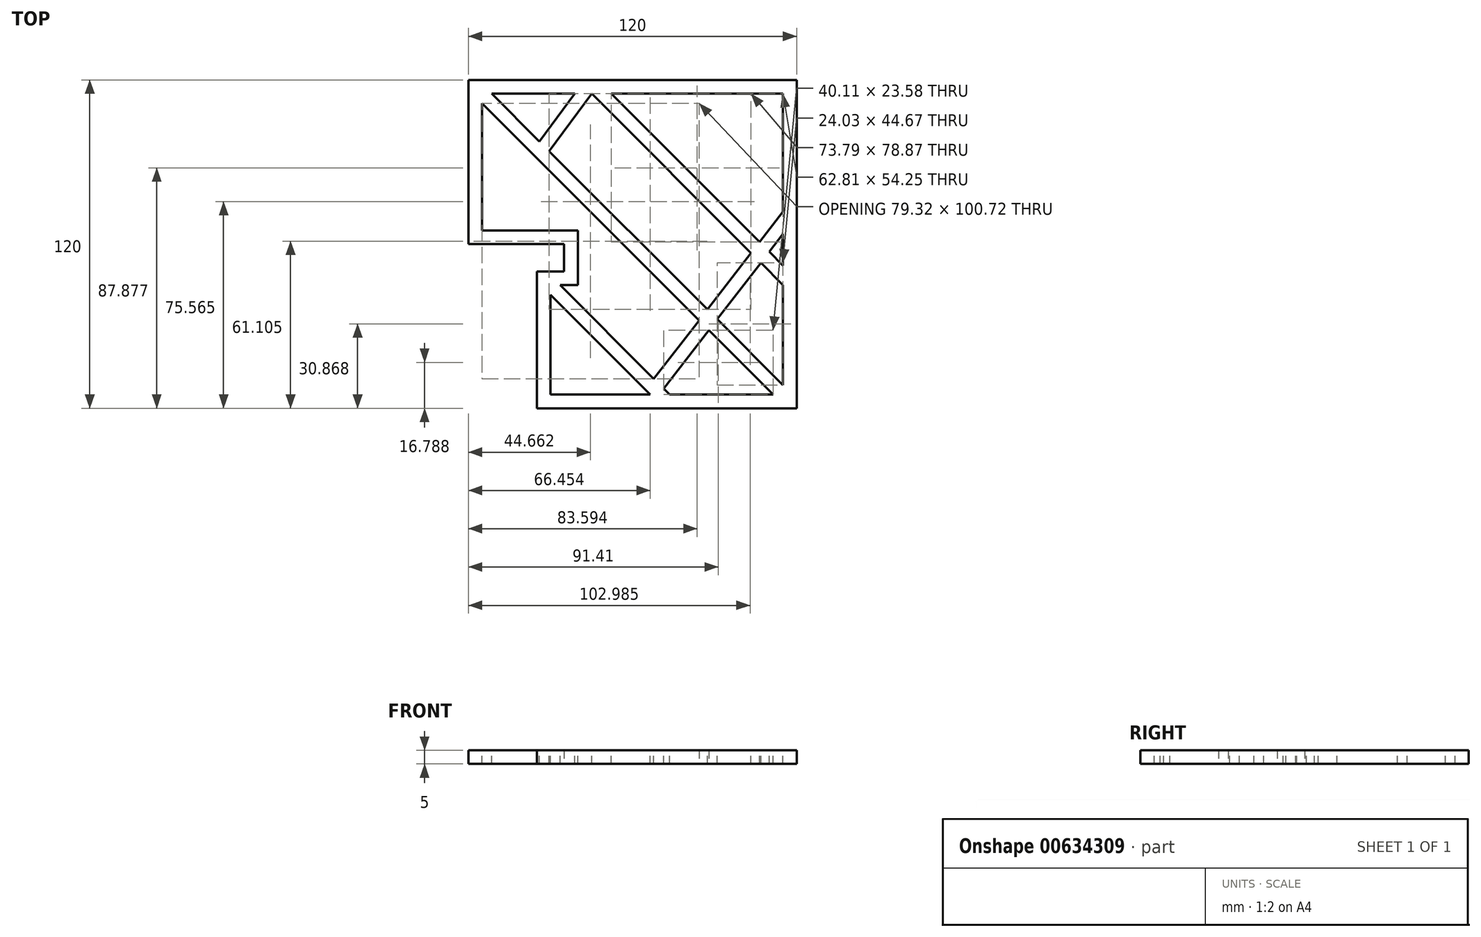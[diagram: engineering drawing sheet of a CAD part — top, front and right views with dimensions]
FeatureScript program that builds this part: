
annotation { "Feature Type Name" : "Feature", "Feature Type Description" : "" }
export const myFeature = defineFeature(function(context is Context, id is Id, definition is map)
    precondition{}
    {
        {
            var Q0;
            Q0=qCreatedBy(makeId("Top.planeOp"),FACE);
            var sketch = newSketch(context, id + "F0", { "sketchPlane" : qUnion([Q0])});
            skLineSegment(sketch, "E0", {"start": v(0, 120) * mm, "end": v(120, 120) * mm});
            skLineSegment(sketch, "E1", {"start": v(120, 120) * mm, "end": v(120, 0) * mm});
            skLineSegment(sketch, "E2", {"start": v(120, 0) * mm, "end": v(25, 0) * mm});
            skLineSegment(sketch, "E3", {"start": v(25, 0) * mm, "end": v(25, 50) * mm});
            skLineSegment(sketch, "E4", {"start": v(25, 50) * mm, "end": v(35, 50) * mm});
            skLineSegment(sketch, "E5", {"start": v(35, 50) * mm, "end": v(35, 60) * mm});
            skLineSegment(sketch, "E6", {"start": v(35, 60) * mm, "end": v(0, 60) * mm});
            skLineSegment(sketch, "E7", {"start": v(0, 60) * mm, "end": v(0, 120) * mm});
            skSolve(sketch);
        }
        {
            var Q0;
            Q0=makeQuery(id+"F0.imprint","IMPRINT",FACE,{"disambiguationData":[TD([[makeQuery(id+"F0.imprint","IMPRINT",EDGE,{"derivedFrom":sQuery(id+"F0.wireOp",EDGE,"E0")}),-1.0]])]});
            extrude(context, id + "F1", {"entities" : qUnion([Q0]), "depth" : 5 * mm, "offsetDistance" : 25 * mm});
        }
        {
            var Q0;
            Q0=makeQuery(id+"F1.opExtrude","CAP_FACE",FACE,{"disambiguationData":[OSD([sQuery(id+"F0.wireOp",EDGE,"E0"),sQuery(id+"F0.wireOp",EDGE,"E1"),sQuery(id+"F0.wireOp",EDGE,"E2"),sQuery(id+"F0.wireOp",EDGE,"E3"),sQuery(id+"F0.wireOp",EDGE,"E4"),sQuery(id+"F0.wireOp",EDGE,"E5"),sQuery(id+"F0.wireOp",EDGE,"E6"),sQuery(id+"F0.wireOp",EDGE,"E7")])],"isStart":false});
            var sketch = newSketch(context, id + "F2", { "sketchPlane" : qUnion([Q0])});
            skLineSegment(sketch, "E8", {"start": v(5, 65) * mm, "end": v(5, 115) * mm});
            skLineSegment(sketch, "E9", {"start": v(5, 115) * mm, "end": v(115, 115) * mm});
            skLineSegment(sketch, "E10", {"start": v(115, 115) * mm, "end": v(115, 5) * mm});
            skLineSegment(sketch, "E11", {"start": v(115, 5) * mm, "end": v(30, 5) * mm});
            skLineSegment(sketch, "E12", {"start": v(30, 5) * mm, "end": v(30, 45) * mm});
            skLineSegment(sketch, "E13", {"start": v(30, 45) * mm, "end": v(40, 45) * mm});
            skLineSegment(sketch, "E14", {"start": v(40, 45) * mm, "end": v(40, 65) * mm});
            skLineSegment(sketch, "E15", {"start": v(40, 65) * mm, "end": v(5, 65) * mm});
            skLineSegment(sketch, "E16", {"start": v(0, 91.25) * mm, "end": v(5, 91.25) * mm, "construction": true});
            skLineSegment(sketch, "E17", {"start": v(21.86, 60) * mm, "end": v(21.86, 65) * mm, "construction": true});
            skLineSegment(sketch, "E18", {"start": v(35, 55) * mm, "end": v(40, 55) * mm, "construction": true});
            skLineSegment(sketch, "E19", {"start": v(54.24, 5) * mm, "end": v(54.24, 0) * mm, "construction": true});
            skLineSegment(sketch, "E20", {"start": v(30, 25) * mm, "end": v(25, 25) * mm, "construction": true});
            skLineSegment(sketch, "E21", {"start": v(115, 35.05) * mm, "end": v(120, 35.05) * mm, "construction": true});
            skLineSegment(sketch, "E22", {"start": v(54.95, 115) * mm, "end": v(54.95, 120) * mm, "construction": true});
            skSolve(sketch);
        }
        {
            var Q0;
            Q0=makeQuery(id+"F2.imprint","IMPRINT",FACE,{"disambiguationData":[TD([[makeQuery(id+"F2.imprint","IMPRINT",EDGE,{"derivedFrom":sQuery(id+"F2.wireOp",EDGE,"E8")}),-1.0]])]});
            extrude(context, id + "F3", {"entities" : qUnion([Q0]), "operationType" : NewBodyOperationType.REMOVE, "oppositeDirection" : true, "depth" : 25 * mm, "offsetDistance" : 25 * mm});
        }
        {
            var Q0;
            Q0=makeQuery(id+"F1.opExtrude","CAP_FACE",FACE,{"disambiguationData":[OSD([sQuery(id+"F0.wireOp",EDGE,"E0"),sQuery(id+"F0.wireOp",EDGE,"E1"),sQuery(id+"F0.wireOp",EDGE,"E2"),sQuery(id+"F0.wireOp",EDGE,"E3"),sQuery(id+"F0.wireOp",EDGE,"E4"),sQuery(id+"F0.wireOp",EDGE,"E5"),sQuery(id+"F0.wireOp",EDGE,"E6"),sQuery(id+"F0.wireOp",EDGE,"E7")])],"isStart":false});
            var sketch = newSketch(context, id + "F4", { "sketchPlane" : qUnion([Q0])});
            skLineSegment(sketch, "E23", {"start": v(115, 5) * mm, "end": v(5, 115) * mm, "construction": true});
            skLineSegment(sketch, "E24", {"start": v(8.54, 115) * mm, "end": v(115, 8.54) * mm});
            skLineSegment(sketch, "E25", {"start": v(115, 8.54) * mm, "end": v(115, 5) * mm});
            skLineSegment(sketch, "E26", {"start": v(111.46, 5) * mm, "end": v(5, 111.46) * mm});
            skLineSegment(sketch, "E27", {"start": v(5, 111.46) * mm, "end": v(5, 115) * mm});
            skLineSegment(sketch, "E28", {"start": v(8.54, 115) * mm, "end": v(6.77, 113.23) * mm, "construction": true});
            skLineSegment(sketch, "E29", {"start": v(6.77, 113.23) * mm, "end": v(5, 111.46) * mm, "construction": true});
            skSolve(sketch);
        }
        {
            var Q0;
            {var subQ3=sQuery(id+"F4.wireOp",EDGE,"E24");Q0=makeQuery(id+"F4.imprint","IMPRINT",FACE,{"disambiguationData":[TD([[makeQuery(id+"F4.imprint","IMPRINT",EDGE,{"derivedFrom":subQ3}),-1.0]])]});}
            extrude(context, id + "F5", {"entities" : qUnion([Q0]), "operationType" : NewBodyOperationType.ADD, "oppositeDirection" : true, "depth" : 5 * mm, "offsetDistance" : 25 * mm});
        }
        {
            var Q0;
            Q0=makeQuery(id+"F5.boolean.opBoolean","MERGE",FACE,{"derivedFrom":[makeQuery(id+"F1.opExtrude","CAP_FACE",FACE,{"disambiguationData":[OSD([sQuery(id+"F0.wireOp",EDGE,"E0"),sQuery(id+"F0.wireOp",EDGE,"E1"),sQuery(id+"F0.wireOp",EDGE,"E2"),sQuery(id+"F0.wireOp",EDGE,"E3"),sQuery(id+"F0.wireOp",EDGE,"E4"),sQuery(id+"F0.wireOp",EDGE,"E5"),sQuery(id+"F0.wireOp",EDGE,"E6"),sQuery(id+"F0.wireOp",EDGE,"E7")])],"isStart":false}),makeQuery(id+"F5.opExtrude","CAP_FACE",FACE,{"disambiguationData":[OSD([sQuery(id+"F2.wireOp",EDGE,"E9"),sQuery(id+"F2.wireOp",EDGE,"E11"),sQuery(id+"F4.wireOp",EDGE,"E24"),sQuery(id+"F4.wireOp",EDGE,"E25"),sQuery(id+"F4.wireOp",EDGE,"E26"),sQuery(id+"F4.wireOp",EDGE,"E27")])],"isStart":true})]});
            var sketch = newSketch(context, id + "F6", { "sketchPlane" : qUnion([Q0])});
            skLineSegment(sketch, "E30", {"start": v(30, 5) * mm, "end": v(115, 115) * mm, "construction": true});
            skLineSegment(sketch, "E31", {"start": v(115, 110.91) * mm, "end": v(33.16, 5) * mm});
            skLineSegment(sketch, "E32", {"start": v(30, 9.09) * mm, "end": v(111.84, 115) * mm});
            skLineSegment(sketch, "E33", {"start": v(82.56, 77.11) * mm, "end": v(84.54, 75.58) * mm, "construction": true});
            skLineSegment(sketch, "E34", {"start": v(84.54, 75.58) * mm, "end": v(86.52, 74.05) * mm, "construction": true});
            skSolve(sketch);
        }
        {
            var Q0;
            {var subQ0=makeQuery(id+"F3.boolean.opBoolean","COPY",EDGE,{"derivedFrom":makeQuery(id+"F3.opExtrude","CAP_EDGE",EDGE,{"disambiguationData":[OSD([sQuery(id+"F2.wireOp",EDGE,"E10")])],"isStart":true})});var subQ5=sQuery(id+"F6.wireOp",EDGE,"E31");var subQ9=makeQuery(id+"F6.imprint","INTERSECT",VERTEX,{"derivedFrom":[subQ0,subQ5]});Q0=makeQuery(id+"F6.imprint","IMPRINT",FACE,{"disambiguationData":[TD([[makeQuery(id+"F6.imprint","IMPRINT",EDGE,{"disambiguationData":[TD([[subQ9,-1.0]])],"derivedFrom":subQ5}),-1.0]])]});}
            var Q1;
            {var subQ0=sQuery(id+"F6.wireOp",EDGE,"E31");var subQ1=makeQuery(id+"F5.opExtrude","CAP_EDGE",EDGE,{"disambiguationData":[OSD([sQuery(id+"F4.wireOp",EDGE,"E24")])],"isStart":true});var subQ2=makeQuery(id+"F6.imprint","INTERSECT",VERTEX,{"derivedFrom":[subQ1,subQ0]});Q1=makeQuery(id+"F6.imprint","IMPRINT",FACE,{"disambiguationData":[TD([[makeQuery(id+"F6.imprint","IMPRINT",EDGE,{"disambiguationData":[TD([[subQ2,-1.0]])],"derivedFrom":subQ0}),-1.0]])]});}
            var Q2;
            {var subQ0=sQuery(id+"F6.wireOp",EDGE,"E31");var subQ7=makeQuery(id+"F3.boolean.opBoolean","COPY",EDGE,{"derivedFrom":makeQuery(id+"F3.opExtrude","CAP_EDGE",EDGE,{"disambiguationData":[OSD([sQuery(id+"F2.wireOp",EDGE,"E11")])],"isStart":true})});var subQ9=makeQuery(id+"F6.imprint","INTERSECT",VERTEX,{"derivedFrom":[subQ7,subQ0]});Q2=makeQuery(id+"F6.imprint","IMPRINT",FACE,{"disambiguationData":[TD([[makeQuery(id+"F6.imprint","IMPRINT",EDGE,{"disambiguationData":[TD([[subQ9,1.0]])],"derivedFrom":subQ0}),-1.0]])]});}
            extrude(context, id + "F7", {"entities" : qUnion([Q0, Q1, Q2]), "operationType" : NewBodyOperationType.ADD, "oppositeDirection" : true, "depth" : 5 * mm, "offsetDistance" : 25 * mm});
        }
        {
            var Q0;
            {var subQ0=sQuery(id+"F2.wireOp",EDGE,"E11");var subQ1=sQuery(id+"F2.wireOp",EDGE,"E9");Q0=makeQuery(id+"F7.boolean.opBoolean","MERGE",FACE,{"derivedFrom":[makeQuery(id+"F5.boolean.opBoolean","MERGE",FACE,{"derivedFrom":[makeQuery(id+"F1.opExtrude","CAP_FACE",FACE,{"disambiguationData":[OSD([sQuery(id+"F0.wireOp",EDGE,"E0"),sQuery(id+"F0.wireOp",EDGE,"E1"),sQuery(id+"F0.wireOp",EDGE,"E2"),sQuery(id+"F0.wireOp",EDGE,"E3"),sQuery(id+"F0.wireOp",EDGE,"E4"),sQuery(id+"F0.wireOp",EDGE,"E5"),sQuery(id+"F0.wireOp",EDGE,"E6"),sQuery(id+"F0.wireOp",EDGE,"E7")])],"isStart":false}),makeQuery(id+"F5.opExtrude","CAP_FACE",FACE,{"disambiguationData":[OSD([subQ1,subQ0,sQuery(id+"F4.wireOp",EDGE,"E24"),sQuery(id+"F4.wireOp",EDGE,"E25"),sQuery(id+"F4.wireOp",EDGE,"E26"),sQuery(id+"F4.wireOp",EDGE,"E27")])],"isStart":true})]}),makeQuery(id+"F7.opExtrude","CAP_FACE",FACE,{"disambiguationData":[OSD([subQ1,sQuery(id+"F2.wireOp",EDGE,"E10"),subQ0,sQuery(id+"F2.wireOp",EDGE,"E12"),sQuery(id+"F6.wireOp",EDGE,"E31"),sQuery(id+"F6.wireOp",EDGE,"E32")])],"isStart":true})]});}
            var sketch = newSketch(context, id + "F8", { "sketchPlane" : qUnion([Q0])});
            skLineSegment(sketch, "E35", {"start": v(40, 65) * mm, "end": v(78.64, 115) * mm, "construction": true});
            skLineSegment(sketch, "E36", {"start": v(40, 60.91) * mm, "end": v(81.8, 115) * mm});
            skLineSegment(sketch, "E37", {"start": v(75.48, 115) * mm, "end": v(36.84, 65) * mm});
            skLineSegment(sketch, "E38", {"start": v(65.07, 97.45) * mm, "end": v(67.05, 95.92) * mm, "construction": true});
            skLineSegment(sketch, "E39", {"start": v(61.65, 97.1) * mm, "end": v(63.63, 95.57) * mm, "construction": true});
            skSolve(sketch);
        }
        {
            var Q0;
            {var subQ0=sQuery(id+"F8.wireOp",EDGE,"E36");var subQ1=sQuery(id+"F2.wireOp",EDGE,"E9");var subQ2=makeQuery(id+"F3.boolean.opBoolean","COPY",EDGE,{"derivedFrom":makeQuery(id+"F3.opExtrude","CAP_EDGE",EDGE,{"disambiguationData":[OSD([subQ1])],"isStart":true})});var subQ3=makeQuery(id+"F8.imprint","INTERSECT",VERTEX,{"derivedFrom":[subQ2,subQ0]});Q0=makeQuery(id+"F8.imprint","IMPRINT",FACE,{"disambiguationData":[TD([[makeQuery(id+"F8.imprint","IMPRINT",EDGE,{"disambiguationData":[TD([[subQ3,1.0]])],"derivedFrom":subQ2}),-1.0]])]});}
            var Q1;
            {var subQ0=sQuery(id+"F8.wireOp",EDGE,"E36");var subQ1=sQuery(id+"F4.wireOp",EDGE,"E26");var subQ10=makeQuery(id+"F7.boolean.opBoolean","SPLIT",EDGE,{"disambiguationData":[TD([makeQuery(id+"F3.boolean.opBoolean","COPY",FACE,{"derivedFrom":makeQuery(id+"F3.opExtrude","SWEPT_FACE",FACE,{"disambiguationData":[OSD([sQuery(id+"F2.wireOp",EDGE,"E8")])]})})])],"derivedFrom":makeQuery(id+"F5.opExtrude","CAP_EDGE",EDGE,{"disambiguationData":[OSD([subQ1])],"isStart":true})});var subQ11=makeQuery(id+"F8.imprint","INTERSECT",VERTEX,{"derivedFrom":[subQ10,subQ0]});Q1=makeQuery(id+"F8.imprint","IMPRINT",FACE,{"disambiguationData":[TD([[makeQuery(id+"F8.imprint","IMPRINT",EDGE,{"disambiguationData":[TD([[subQ11,-1.0]])],"derivedFrom":subQ0}),1.0]])]});}
            var Q2;
            {var subQ0=makeQuery(id+"F3.boolean.opBoolean","COPY",EDGE,{"derivedFrom":makeQuery(id+"F3.opExtrude","CAP_EDGE",EDGE,{"disambiguationData":[OSD([sQuery(id+"F2.wireOp",EDGE,"E15")])],"isStart":true})});var subQ1=makeQuery(id+"F3.boolean.opBoolean","COPY",EDGE,{"derivedFrom":makeQuery(id+"F3.opExtrude","CAP_EDGE",EDGE,{"disambiguationData":[OSD([sQuery(id+"F2.wireOp",EDGE,"E14")])],"isStart":true})});var subQ2=makeQuery(id+"F8.imprint","INTERSECT",VERTEX,{"derivedFrom":[subQ1,subQ0]});Q2=makeQuery(id+"F8.imprint","IMPRINT",FACE,{"disambiguationData":[TD([[makeQuery(id+"F8.imprint","IMPRINT",EDGE,{"disambiguationData":[TD([[subQ2,1.0]])],"derivedFrom":subQ1}),-1.0]])]});}
            extrude(context, id + "F9", {"entities" : qUnion([Q0, Q1, Q2]), "operationType" : NewBodyOperationType.ADD, "oppositeDirection" : true, "depth" : 5 * mm, "offsetDistance" : 25 * mm});
        }
        {
            var Q0;
            {var subQ0=sQuery(id+"F2.wireOp",EDGE,"E9");var subQ1=sQuery(id+"F2.wireOp",EDGE,"E11");Q0=makeQuery(id+"F9.boolean.opBoolean","MERGE",FACE,{"derivedFrom":[makeQuery(id+"F7.boolean.opBoolean","MERGE",FACE,{"derivedFrom":[makeQuery(id+"F5.boolean.opBoolean","MERGE",FACE,{"derivedFrom":[makeQuery(id+"F1.opExtrude","CAP_FACE",FACE,{"disambiguationData":[OSD([sQuery(id+"F0.wireOp",EDGE,"E0"),sQuery(id+"F0.wireOp",EDGE,"E1"),sQuery(id+"F0.wireOp",EDGE,"E2"),sQuery(id+"F0.wireOp",EDGE,"E3"),sQuery(id+"F0.wireOp",EDGE,"E4"),sQuery(id+"F0.wireOp",EDGE,"E5"),sQuery(id+"F0.wireOp",EDGE,"E6"),sQuery(id+"F0.wireOp",EDGE,"E7")])],"isStart":false}),makeQuery(id+"F5.opExtrude","CAP_FACE",FACE,{"disambiguationData":[OSD([subQ0,subQ1,sQuery(id+"F4.wireOp",EDGE,"E24"),sQuery(id+"F4.wireOp",EDGE,"E25"),sQuery(id+"F4.wireOp",EDGE,"E26"),sQuery(id+"F4.wireOp",EDGE,"E27")])],"isStart":true})]}),makeQuery(id+"F7.opExtrude","CAP_FACE",FACE,{"disambiguationData":[OSD([subQ0,sQuery(id+"F2.wireOp",EDGE,"E10"),subQ1,sQuery(id+"F2.wireOp",EDGE,"E12"),sQuery(id+"F6.wireOp",EDGE,"E31"),sQuery(id+"F6.wireOp",EDGE,"E32")])],"isStart":true})]}),makeQuery(id+"F9.opExtrude","CAP_FACE",FACE,{"disambiguationData":[OSD([subQ0,sQuery(id+"F2.wireOp",EDGE,"E14"),sQuery(id+"F2.wireOp",EDGE,"E15"),sQuery(id+"F8.wireOp",EDGE,"E36"),sQuery(id+"F8.wireOp",EDGE,"E37")])],"isStart":true})]});}
            var sketch = newSketch(context, id + "F10", { "sketchPlane" : qUnion([Q0])});
            skLineSegment(sketch, "E40", {"start": v(5, 65) * mm, "end": v(42, 115) * mm, "construction": true});
            skLineSegment(sketch, "E41", {"start": v(8.11, 65) * mm, "end": v(45.12, 115) * mm});
            skLineSegment(sketch, "E42", {"start": v(5, 69.2) * mm, "end": v(38.9, 115) * mm});
            skLineSegment(sketch, "E43", {"start": v(20.4, 90) * mm, "end": v(22.4, 88.52) * mm, "construction": true});
            skLineSegment(sketch, "E44", {"start": v(22.4, 88.52) * mm, "end": v(24.42, 87.03) * mm, "construction": true});
            skSolve(sketch);
        }
        {
            var Q0;
            {var subQ0=sQuery(id+"F10.wireOp",EDGE,"E41");var subQ1=sQuery(id+"F4.wireOp",EDGE,"E24");var subQ3=sQuery(id+"F2.wireOp",EDGE,"E9");var subQ6=makeQuery(id+"F5.opExtrude","SWEPT_FACE",FACE,{"disambiguationData":[OSD([subQ1])]});var subQ13=makeQuery(id+"F9.boolean.opBoolean","SPLIT",EDGE,{"disambiguationData":[TD([subQ6])],"derivedFrom":makeQuery(id+"F3.boolean.opBoolean","COPY",EDGE,{"derivedFrom":makeQuery(id+"F3.opExtrude","CAP_EDGE",EDGE,{"disambiguationData":[OSD([subQ3])],"isStart":true})})});var subQ14=makeQuery(id+"F10.imprint","INTERSECT",VERTEX,{"derivedFrom":[subQ13,subQ0]});Q0=makeQuery(id+"F10.imprint","IMPRINT",FACE,{"disambiguationData":[TD([[makeQuery(id+"F10.imprint","IMPRINT",EDGE,{"disambiguationData":[TD([[subQ14,1.0]])],"derivedFrom":subQ0}),1.0]])]});}
            var Q1;
            {var subQ0=sQuery(id+"F10.wireOp",EDGE,"E41");var subQ1=sQuery(id+"F4.wireOp",EDGE,"E26");var subQ7=makeQuery(id+"F3.boolean.opBoolean","COPY",FACE,{"derivedFrom":makeQuery(id+"F3.opExtrude","SWEPT_FACE",FACE,{"disambiguationData":[OSD([sQuery(id+"F2.wireOp",EDGE,"E8")])]})});var subQ15=makeQuery(id+"F9.boolean.opBoolean","SPLIT",EDGE,{"disambiguationData":[TD([subQ7])],"derivedFrom":makeQuery(id+"F7.boolean.opBoolean","SPLIT",EDGE,{"disambiguationData":[TD([subQ7])],"derivedFrom":makeQuery(id+"F5.opExtrude","CAP_EDGE",EDGE,{"disambiguationData":[OSD([subQ1])],"isStart":true})})});var subQ16=makeQuery(id+"F10.imprint","INTERSECT",VERTEX,{"derivedFrom":[subQ15,subQ0]});Q1=makeQuery(id+"F10.imprint","IMPRINT",FACE,{"disambiguationData":[TD([[makeQuery(id+"F10.imprint","IMPRINT",EDGE,{"disambiguationData":[TD([[subQ16,-1.0]])],"derivedFrom":subQ0}),1.0]])]});}
            var Q2;
            {var subQ0=sQuery(id+"F2.wireOp",EDGE,"E15");var subQ1=makeQuery(id+"F3.boolean.opBoolean","COPY",EDGE,{"derivedFrom":makeQuery(id+"F3.opExtrude","CAP_EDGE",EDGE,{"disambiguationData":[OSD([subQ0])],"isStart":true})});var subQ2=sQuery(id+"F2.wireOp",EDGE,"E8");var subQ3=makeQuery(id+"F3.boolean.opBoolean","COPY",EDGE,{"derivedFrom":makeQuery(id+"F3.opExtrude","CAP_EDGE",EDGE,{"disambiguationData":[OSD([subQ2])],"isStart":true})});var subQ4=makeQuery(id+"F10.imprint","INTERSECT",VERTEX,{"derivedFrom":[subQ3,subQ1]});Q2=makeQuery(id+"F10.imprint","IMPRINT",FACE,{"disambiguationData":[TD([[makeQuery(id+"F10.imprint","IMPRINT",EDGE,{"disambiguationData":[TD([[subQ4,-1.0]])],"derivedFrom":subQ3}),-1.0]])]});}
            extrude(context, id + "F11", {"entities" : qUnion([Q0, Q1, Q2]), "operationType" : NewBodyOperationType.ADD, "oppositeDirection" : true, "depth" : 5 * mm, "offsetDistance" : 25 * mm});
        }
        {
            var Q0;
            {var subQ0=sQuery(id+"F2.wireOp",EDGE,"E15");var subQ1=sQuery(id+"F2.wireOp",EDGE,"E9");var subQ2=sQuery(id+"F2.wireOp",EDGE,"E11");Q0=makeQuery(id+"F11.boolean.opBoolean","MERGE",FACE,{"derivedFrom":[makeQuery(id+"F9.boolean.opBoolean","MERGE",FACE,{"derivedFrom":[makeQuery(id+"F7.boolean.opBoolean","MERGE",FACE,{"derivedFrom":[makeQuery(id+"F5.boolean.opBoolean","MERGE",FACE,{"derivedFrom":[makeQuery(id+"F1.opExtrude","CAP_FACE",FACE,{"disambiguationData":[OSD([sQuery(id+"F0.wireOp",EDGE,"E0"),sQuery(id+"F0.wireOp",EDGE,"E1"),sQuery(id+"F0.wireOp",EDGE,"E2"),sQuery(id+"F0.wireOp",EDGE,"E3"),sQuery(id+"F0.wireOp",EDGE,"E4"),sQuery(id+"F0.wireOp",EDGE,"E5"),sQuery(id+"F0.wireOp",EDGE,"E6"),sQuery(id+"F0.wireOp",EDGE,"E7")])],"isStart":false}),makeQuery(id+"F5.opExtrude","CAP_FACE",FACE,{"disambiguationData":[OSD([subQ1,subQ2,sQuery(id+"F4.wireOp",EDGE,"E24"),sQuery(id+"F4.wireOp",EDGE,"E25"),sQuery(id+"F4.wireOp",EDGE,"E26"),sQuery(id+"F4.wireOp",EDGE,"E27")])],"isStart":true})]}),makeQuery(id+"F7.opExtrude","CAP_FACE",FACE,{"disambiguationData":[OSD([subQ1,sQuery(id+"F2.wireOp",EDGE,"E10"),subQ2,sQuery(id+"F2.wireOp",EDGE,"E12"),sQuery(id+"F6.wireOp",EDGE,"E31"),sQuery(id+"F6.wireOp",EDGE,"E32")])],"isStart":true})]}),makeQuery(id+"F9.opExtrude","CAP_FACE",FACE,{"disambiguationData":[OSD([subQ1,sQuery(id+"F2.wireOp",EDGE,"E14"),subQ0,sQuery(id+"F8.wireOp",EDGE,"E36"),sQuery(id+"F8.wireOp",EDGE,"E37")])],"isStart":true})]}),makeQuery(id+"F11.opExtrude","CAP_FACE",FACE,{"disambiguationData":[OSD([sQuery(id+"F2.wireOp",EDGE,"E8"),subQ1,subQ0,sQuery(id+"F10.wireOp",EDGE,"E41"),sQuery(id+"F10.wireOp",EDGE,"E42")])],"isStart":true})]});}
            var sketch = newSketch(context, id + "F12", { "sketchPlane" : qUnion([Q0])});
            skLineSegment(sketch, "E45", {"start": v(30, 45) * mm, "end": v(70, 5) * mm, "construction": true});
            skLineSegment(sketch, "E46", {"start": v(30, 41.46) * mm, "end": v(66.46, 5) * mm});
            skLineSegment(sketch, "E47", {"start": v(39.27, 35.73) * mm, "end": v(37.5, 33.96) * mm, "construction": true});
            skLineSegment(sketch, "E48", {"start": v(33.54, 45) * mm, "end": v(73.54, 5) * mm});
            skLineSegment(sketch, "E49", {"start": v(44.11, 34.42) * mm, "end": v(42.34, 32.66) * mm, "construction": true});
            skSolve(sketch);
        }
        {
            var Q0;
            {var subQ0=sQuery(id+"F2.wireOp",EDGE,"E12");var subQ1=makeQuery(id+"F3.boolean.opBoolean","COPY",EDGE,{"derivedFrom":makeQuery(id+"F3.opExtrude","CAP_EDGE",EDGE,{"disambiguationData":[OSD([subQ0])],"isStart":true})});var subQ2=makeQuery(id+"F3.boolean.opBoolean","COPY",EDGE,{"derivedFrom":makeQuery(id+"F3.opExtrude","CAP_EDGE",EDGE,{"disambiguationData":[OSD([sQuery(id+"F2.wireOp",EDGE,"E13")])],"isStart":true})});var subQ3=makeQuery(id+"F12.imprint","INTERSECT",VERTEX,{"derivedFrom":[subQ2,subQ1]});Q0=makeQuery(id+"F12.imprint","IMPRINT",FACE,{"disambiguationData":[TD([[makeQuery(id+"F12.imprint","IMPRINT",EDGE,{"disambiguationData":[TD([[subQ3,-1.0]])],"derivedFrom":subQ2}),-1.0]])]});}
            var Q1;
            {var subQ0=sQuery(id+"F12.wireOp",EDGE,"E46");var subQ6=sQuery(id+"F2.wireOp",EDGE,"E12");var subQ8=sQuery(id+"F6.wireOp",EDGE,"E32");var subQ11=makeQuery(id+"F7.boolean.opBoolean","SPLIT",EDGE,{"disambiguationData":[TD([makeQuery(id+"F3.boolean.opBoolean","COPY",FACE,{"derivedFrom":makeQuery(id+"F3.opExtrude","SWEPT_FACE",FACE,{"disambiguationData":[OSD([subQ6])]})})])],"derivedFrom":makeQuery(id+"F7.opExtrude","CAP_EDGE",EDGE,{"disambiguationData":[OSD([subQ8])],"isStart":true})});var subQ12=makeQuery(id+"F12.imprint","INTERSECT",VERTEX,{"derivedFrom":[subQ11,subQ0]});Q1=makeQuery(id+"F12.imprint","IMPRINT",FACE,{"disambiguationData":[TD([[makeQuery(id+"F12.imprint","IMPRINT",EDGE,{"disambiguationData":[TD([[subQ12,-1.0]])],"derivedFrom":subQ0}),1.0]])]});}
            var Q2;
            {var subQ0=sQuery(id+"F12.wireOp",EDGE,"E46");var subQ1=sQuery(id+"F2.wireOp",EDGE,"E11");var subQ2=makeQuery(id+"F3.boolean.opBoolean","COPY",EDGE,{"derivedFrom":makeQuery(id+"F3.opExtrude","CAP_EDGE",EDGE,{"disambiguationData":[OSD([subQ1])],"isStart":true})});var subQ3=makeQuery(id+"F12.imprint","INTERSECT",VERTEX,{"derivedFrom":[subQ2,subQ0]});Q2=makeQuery(id+"F12.imprint","IMPRINT",FACE,{"disambiguationData":[TD([[makeQuery(id+"F12.imprint","IMPRINT",EDGE,{"disambiguationData":[TD([[subQ3,1.0]])],"derivedFrom":subQ2}),-1.0]])]});}
            extrude(context, id + "F13", {"entities" : qUnion([Q0, Q1, Q2]), "operationType" : NewBodyOperationType.ADD, "oppositeDirection" : true, "depth" : 5 * mm, "offsetDistance" : 25 * mm});
        }
        {
            var Q0;
            {var subQ0=sQuery(id+"F2.wireOp",EDGE,"E12");var subQ1=sQuery(id+"F2.wireOp",EDGE,"E11");var subQ2=sQuery(id+"F2.wireOp",EDGE,"E15");var subQ3=sQuery(id+"F2.wireOp",EDGE,"E9");Q0=makeQuery(id+"F13.boolean.opBoolean","MERGE",FACE,{"derivedFrom":[makeQuery(id+"F11.boolean.opBoolean","MERGE",FACE,{"derivedFrom":[makeQuery(id+"F9.boolean.opBoolean","MERGE",FACE,{"derivedFrom":[makeQuery(id+"F7.boolean.opBoolean","MERGE",FACE,{"derivedFrom":[makeQuery(id+"F5.boolean.opBoolean","MERGE",FACE,{"derivedFrom":[makeQuery(id+"F1.opExtrude","CAP_FACE",FACE,{"disambiguationData":[OSD([sQuery(id+"F0.wireOp",EDGE,"E0"),sQuery(id+"F0.wireOp",EDGE,"E1"),sQuery(id+"F0.wireOp",EDGE,"E2"),sQuery(id+"F0.wireOp",EDGE,"E3"),sQuery(id+"F0.wireOp",EDGE,"E4"),sQuery(id+"F0.wireOp",EDGE,"E5"),sQuery(id+"F0.wireOp",EDGE,"E6"),sQuery(id+"F0.wireOp",EDGE,"E7")])],"isStart":false}),makeQuery(id+"F5.opExtrude","CAP_FACE",FACE,{"disambiguationData":[OSD([subQ3,subQ1,sQuery(id+"F4.wireOp",EDGE,"E24"),sQuery(id+"F4.wireOp",EDGE,"E25"),sQuery(id+"F4.wireOp",EDGE,"E26"),sQuery(id+"F4.wireOp",EDGE,"E27")])],"isStart":true})]}),makeQuery(id+"F7.opExtrude","CAP_FACE",FACE,{"disambiguationData":[OSD([subQ3,sQuery(id+"F2.wireOp",EDGE,"E10"),subQ1,subQ0,sQuery(id+"F6.wireOp",EDGE,"E31"),sQuery(id+"F6.wireOp",EDGE,"E32")])],"isStart":true})]}),makeQuery(id+"F9.opExtrude","CAP_FACE",FACE,{"disambiguationData":[OSD([subQ3,sQuery(id+"F2.wireOp",EDGE,"E14"),subQ2,sQuery(id+"F8.wireOp",EDGE,"E36"),sQuery(id+"F8.wireOp",EDGE,"E37")])],"isStart":true})]}),makeQuery(id+"F11.opExtrude","CAP_FACE",FACE,{"disambiguationData":[OSD([sQuery(id+"F2.wireOp",EDGE,"E8"),subQ3,subQ2,sQuery(id+"F10.wireOp",EDGE,"E41"),sQuery(id+"F10.wireOp",EDGE,"E42")])],"isStart":true})]}),makeQuery(id+"F13.opExtrude","CAP_FACE",FACE,{"disambiguationData":[OSD([subQ1,subQ0,sQuery(id+"F2.wireOp",EDGE,"E13"),sQuery(id+"F12.wireOp",EDGE,"E46"),sQuery(id+"F12.wireOp",EDGE,"E48")])],"isStart":true})]});}
            var sketch = newSketch(context, id + "F14", { "sketchPlane" : qUnion([Q0])});
            skLineSegment(sketch, "E50", {"start": v(45.12, 115) * mm, "end": v(115, 45.12) * mm});
            skLineSegment(sketch, "E51", {"start": v(52.19, 115) * mm, "end": v(115, 52.19) * mm});
            skLineSegment(sketch, "E52", {"start": v(55.3, 104.82) * mm, "end": v(58.83, 108.36) * mm, "construction": true});
            skSolve(sketch);
        }
        {
            var Q0;
            {var subQ0=sQuery(id+"F14.wireOp",EDGE,"E50");var subQ3=sQuery(id+"F2.wireOp",EDGE,"E9");var subQ5=makeQuery(id+"F3.boolean.opBoolean","COPY",FACE,{"derivedFrom":makeQuery(id+"F3.opExtrude","SWEPT_FACE",FACE,{"disambiguationData":[OSD([subQ3])]})});var subQ7=sQuery(id+"F8.wireOp",EDGE,"E37");var subQ18=makeQuery(id+"F9.boolean.opBoolean","SPLIT",EDGE,{"disambiguationData":[TD([subQ5])],"derivedFrom":makeQuery(id+"F9.opExtrude","CAP_EDGE",EDGE,{"disambiguationData":[OSD([subQ7])],"isStart":true})});var subQ19=makeQuery(id+"F14.imprint","INTERSECT",VERTEX,{"derivedFrom":[subQ18,subQ0]});Q0=makeQuery(id+"F14.imprint","IMPRINT",FACE,{"disambiguationData":[TD([[makeQuery(id+"F14.imprint","IMPRINT",EDGE,{"disambiguationData":[TD([[subQ19,1.0]])],"derivedFrom":subQ18}),-1.0]])]});}
            var Q1;
            {var subQ0=sQuery(id+"F14.wireOp",EDGE,"E50");var subQ3=sQuery(id+"F2.wireOp",EDGE,"E9");var subQ5=makeQuery(id+"F3.boolean.opBoolean","COPY",FACE,{"derivedFrom":makeQuery(id+"F3.opExtrude","SWEPT_FACE",FACE,{"disambiguationData":[OSD([subQ3])]})});var subQ7=sQuery(id+"F8.wireOp",EDGE,"E37");var subQ12=makeQuery(id+"F9.boolean.opBoolean","SPLIT",EDGE,{"disambiguationData":[TD([subQ5])],"derivedFrom":makeQuery(id+"F9.opExtrude","CAP_EDGE",EDGE,{"disambiguationData":[OSD([subQ7])],"isStart":true})});var subQ13=makeQuery(id+"F14.imprint","INTERSECT",VERTEX,{"derivedFrom":[subQ12,subQ0]});Q1=makeQuery(id+"F14.imprint","IMPRINT",FACE,{"disambiguationData":[TD([[makeQuery(id+"F14.imprint","IMPRINT",EDGE,{"disambiguationData":[TD([[subQ13,-1.0]])],"derivedFrom":subQ0}),1.0]])]});}
            var Q2;
            {var subQ0=sQuery(id+"F14.wireOp",EDGE,"E50");var subQ3=sQuery(id+"F2.wireOp",EDGE,"E9");var subQ5=makeQuery(id+"F3.boolean.opBoolean","COPY",FACE,{"derivedFrom":makeQuery(id+"F3.opExtrude","SWEPT_FACE",FACE,{"disambiguationData":[OSD([subQ3])]})});var subQ9=sQuery(id+"F6.wireOp",EDGE,"E32");var subQ13=makeQuery(id+"F7.boolean.opBoolean","SPLIT",EDGE,{"disambiguationData":[TD([subQ5])],"derivedFrom":makeQuery(id+"F7.opExtrude","CAP_EDGE",EDGE,{"disambiguationData":[OSD([subQ9])],"isStart":true})});var subQ14=makeQuery(id+"F14.imprint","INTERSECT",VERTEX,{"derivedFrom":[subQ13,subQ0]});Q2=makeQuery(id+"F14.imprint","IMPRINT",FACE,{"disambiguationData":[TD([[makeQuery(id+"F14.imprint","IMPRINT",EDGE,{"disambiguationData":[TD([[subQ14,1.0]])],"derivedFrom":subQ0}),1.0]])]});}
            var Q3;
            {var subQ0=sQuery(id+"F14.wireOp",EDGE,"E50");var subQ1=sQuery(id+"F2.wireOp",EDGE,"E10");var subQ2=makeQuery(id+"F3.boolean.opBoolean","COPY",EDGE,{"derivedFrom":makeQuery(id+"F3.opExtrude","CAP_EDGE",EDGE,{"disambiguationData":[OSD([subQ1])],"isStart":true})});var subQ3=makeQuery(id+"F14.imprint","INTERSECT",VERTEX,{"derivedFrom":[subQ2,subQ0]});Q3=makeQuery(id+"F14.imprint","IMPRINT",FACE,{"disambiguationData":[TD([[makeQuery(id+"F14.imprint","IMPRINT",EDGE,{"disambiguationData":[TD([[subQ3,1.0]])],"derivedFrom":subQ2}),-1.0]])]});}
            var Q4;
            {var subQ0=sQuery(id+"F14.wireOp",EDGE,"E50");var subQ3=sQuery(id+"F2.wireOp",EDGE,"E9");var subQ7=sQuery(id+"F6.wireOp",EDGE,"E32");var subQ11=makeQuery(id+"F7.boolean.opBoolean","SPLIT",EDGE,{"disambiguationData":[TD([makeQuery(id+"F3.boolean.opBoolean","COPY",FACE,{"derivedFrom":makeQuery(id+"F3.opExtrude","SWEPT_FACE",FACE,{"disambiguationData":[OSD([subQ3])]})})])],"derivedFrom":makeQuery(id+"F7.opExtrude","CAP_EDGE",EDGE,{"disambiguationData":[OSD([subQ7])],"isStart":true})});var subQ12=makeQuery(id+"F14.imprint","INTERSECT",VERTEX,{"derivedFrom":[subQ11,subQ0]});Q4=makeQuery(id+"F14.imprint","IMPRINT",FACE,{"disambiguationData":[TD([[makeQuery(id+"F14.imprint","IMPRINT",EDGE,{"disambiguationData":[TD([[subQ12,-1.0]])],"derivedFrom":subQ0}),1.0]])]});}
            extrude(context, id + "F15", {"entities" : qUnion([Q0, Q1, Q2, Q3, Q4]), "operationType" : NewBodyOperationType.ADD, "oppositeDirection" : true, "depth" : 5 * mm, "offsetDistance" : 25 * mm});
        }
        {
            var Q0;
            {var subQ0=sQuery(id+"F2.wireOp",EDGE,"E10");var subQ1=sQuery(id+"F2.wireOp",EDGE,"E9");var subQ2=sQuery(id+"F2.wireOp",EDGE,"E12");var subQ3=sQuery(id+"F2.wireOp",EDGE,"E11");var subQ4=sQuery(id+"F2.wireOp",EDGE,"E15");Q0=makeQuery(id+"F15.boolean.opBoolean","MERGE",FACE,{"derivedFrom":[makeQuery(id+"F13.boolean.opBoolean","MERGE",FACE,{"derivedFrom":[makeQuery(id+"F11.boolean.opBoolean","MERGE",FACE,{"derivedFrom":[makeQuery(id+"F9.boolean.opBoolean","MERGE",FACE,{"derivedFrom":[makeQuery(id+"F7.boolean.opBoolean","MERGE",FACE,{"derivedFrom":[makeQuery(id+"F5.boolean.opBoolean","MERGE",FACE,{"derivedFrom":[makeQuery(id+"F1.opExtrude","CAP_FACE",FACE,{"disambiguationData":[OSD([sQuery(id+"F0.wireOp",EDGE,"E0"),sQuery(id+"F0.wireOp",EDGE,"E1"),sQuery(id+"F0.wireOp",EDGE,"E2"),sQuery(id+"F0.wireOp",EDGE,"E3"),sQuery(id+"F0.wireOp",EDGE,"E4"),sQuery(id+"F0.wireOp",EDGE,"E5"),sQuery(id+"F0.wireOp",EDGE,"E6"),sQuery(id+"F0.wireOp",EDGE,"E7")])],"isStart":false}),makeQuery(id+"F5.opExtrude","CAP_FACE",FACE,{"disambiguationData":[OSD([subQ1,subQ3,sQuery(id+"F4.wireOp",EDGE,"E24"),sQuery(id+"F4.wireOp",EDGE,"E25"),sQuery(id+"F4.wireOp",EDGE,"E26"),sQuery(id+"F4.wireOp",EDGE,"E27")])],"isStart":true})]}),makeQuery(id+"F7.opExtrude","CAP_FACE",FACE,{"disambiguationData":[OSD([subQ1,subQ0,subQ3,subQ2,sQuery(id+"F6.wireOp",EDGE,"E31"),sQuery(id+"F6.wireOp",EDGE,"E32")])],"isStart":true})]}),makeQuery(id+"F9.opExtrude","CAP_FACE",FACE,{"disambiguationData":[OSD([subQ1,sQuery(id+"F2.wireOp",EDGE,"E14"),subQ4,sQuery(id+"F8.wireOp",EDGE,"E36"),sQuery(id+"F8.wireOp",EDGE,"E37")])],"isStart":true})]}),makeQuery(id+"F11.opExtrude","CAP_FACE",FACE,{"disambiguationData":[OSD([sQuery(id+"F2.wireOp",EDGE,"E8"),subQ1,subQ4,sQuery(id+"F10.wireOp",EDGE,"E41"),sQuery(id+"F10.wireOp",EDGE,"E42")])],"isStart":true})]}),makeQuery(id+"F13.opExtrude","CAP_FACE",FACE,{"disambiguationData":[OSD([subQ3,subQ2,sQuery(id+"F2.wireOp",EDGE,"E13"),sQuery(id+"F12.wireOp",EDGE,"E46"),sQuery(id+"F12.wireOp",EDGE,"E48")])],"isStart":true})]}),makeQuery(id+"F15.opExtrude","CAP_FACE",FACE,{"disambiguationData":[OSD([subQ1,subQ0,sQuery(id+"F14.wireOp",EDGE,"E50"),sQuery(id+"F14.wireOp",EDGE,"E51")])],"isStart":true})]});}
            var sketch = newSketch(context, id + "F16", { "sketchPlane" : qUnion([Q0])});
            skLineSegment(sketch, "E53", {"start": v(67.8, 10.75) * mm, "end": v(115, 71.84) * mm});
            skLineSegment(sketch, "E54", {"start": v(71.35, 7.18) * mm, "end": v(115, 63.66) * mm});
            skLineSegment(sketch, "E55", {"start": v(50.76, 27.78) * mm, "end": v(67.8, 10.75) * mm, "construction": true});
            skLineSegment(sketch, "E56", {"start": v(115, 71.84) * mm, "end": v(97.97, 88.87) * mm, "construction": true});
            skLineSegment(sketch, "E57", {"start": v(67.8, 10.75) * mm, "end": v(71.35, 7.18) * mm});
            skSolve(sketch);
        }
        {
            var Q0;
            {var subQ0=sQuery(id+"F16.wireOp",EDGE,"E53");var subQ4=sQuery(id+"F2.wireOp",EDGE,"E10");var subQ6=sQuery(id+"F6.wireOp",EDGE,"E31");var subQ7=makeQuery(id+"F7.opExtrude","SWEPT_FACE",FACE,{"disambiguationData":[OSD([subQ6])]});var subQ18=makeQuery(id+"F15.boolean.opBoolean","SPLIT",EDGE,{"disambiguationData":[TD([subQ7])],"derivedFrom":makeQuery(id+"F3.boolean.opBoolean","COPY",EDGE,{"derivedFrom":makeQuery(id+"F3.opExtrude","CAP_EDGE",EDGE,{"disambiguationData":[OSD([subQ4])],"isStart":true})})});var subQ19=makeQuery(id+"F16.imprint","INTERSECT",VERTEX,{"derivedFrom":[subQ18,subQ0]});Q0=makeQuery(id+"F16.imprint","IMPRINT",FACE,{"disambiguationData":[TD([[makeQuery(id+"F16.imprint","IMPRINT",EDGE,{"disambiguationData":[TD([[subQ19,1.0]])],"derivedFrom":subQ0}),-1.0]])]});}
            var Q1;
            {var subQ0=sQuery(id+"F16.wireOp",EDGE,"E53");var subQ4=sQuery(id+"F2.wireOp",EDGE,"E10");var subQ5=makeQuery(id+"F3.boolean.opBoolean","COPY",FACE,{"derivedFrom":makeQuery(id+"F3.opExtrude","SWEPT_FACE",FACE,{"disambiguationData":[OSD([subQ4])]})});var subQ15=sQuery(id+"F14.wireOp",EDGE,"E50");var subQ18=makeQuery(id+"F15.boolean.opBoolean","SPLIT",EDGE,{"disambiguationData":[TD([subQ5])],"derivedFrom":makeQuery(id+"F15.opExtrude","CAP_EDGE",EDGE,{"disambiguationData":[OSD([subQ15])],"isStart":true})});var subQ19=makeQuery(id+"F16.imprint","INTERSECT",VERTEX,{"derivedFrom":[subQ18,subQ0]});Q1=makeQuery(id+"F16.imprint","IMPRINT",FACE,{"disambiguationData":[TD([[makeQuery(id+"F16.imprint","IMPRINT",EDGE,{"disambiguationData":[TD([[subQ19,-1.0]])],"derivedFrom":subQ0}),-1.0]])]});}
            var Q2;
            {var subQ0=sQuery(id+"F16.wireOp",EDGE,"E53");var subQ1=sQuery(id+"F4.wireOp",EDGE,"E24");var subQ5=sQuery(id+"F2.wireOp",EDGE,"E10");var subQ6=makeQuery(id+"F3.boolean.opBoolean","COPY",FACE,{"derivedFrom":makeQuery(id+"F3.opExtrude","SWEPT_FACE",FACE,{"disambiguationData":[OSD([subQ5])]})});var subQ12=makeQuery(id+"F7.boolean.opBoolean","SPLIT",EDGE,{"disambiguationData":[TD([subQ6])],"derivedFrom":makeQuery(id+"F5.opExtrude","CAP_EDGE",EDGE,{"disambiguationData":[OSD([subQ1])],"isStart":true})});var subQ13=makeQuery(id+"F16.imprint","INTERSECT",VERTEX,{"derivedFrom":[subQ12,subQ0]});Q2=makeQuery(id+"F16.imprint","IMPRINT",FACE,{"disambiguationData":[TD([[makeQuery(id+"F16.imprint","IMPRINT",EDGE,{"disambiguationData":[TD([[subQ13,-1.0]])],"derivedFrom":subQ0}),-1.0]])]});}
            var Q3;
            {var subQ0=sQuery(id+"F16.wireOp",EDGE,"E53");var subQ1=sQuery(id+"F4.wireOp",EDGE,"E26");var subQ3=sQuery(id+"F2.wireOp",EDGE,"E11");var subQ11=makeQuery(id+"F7.boolean.opBoolean","SPLIT",EDGE,{"disambiguationData":[TD([makeQuery(id+"F3.boolean.opBoolean","COPY",FACE,{"derivedFrom":makeQuery(id+"F3.opExtrude","SWEPT_FACE",FACE,{"disambiguationData":[OSD([subQ3])]})})])],"derivedFrom":makeQuery(id+"F5.opExtrude","CAP_EDGE",EDGE,{"disambiguationData":[OSD([subQ1])],"isStart":true})});var subQ12=makeQuery(id+"F16.imprint","INTERSECT",VERTEX,{"derivedFrom":[subQ11,subQ0]});Q3=makeQuery(id+"F16.imprint","IMPRINT",FACE,{"disambiguationData":[TD([[makeQuery(id+"F16.imprint","IMPRINT",EDGE,{"disambiguationData":[TD([[subQ12,-1.0]])],"derivedFrom":subQ0}),-1.0]])]});}
            var Q4;
            {var subQ0=sQuery(id+"F16.wireOp",EDGE,"E57");Q4=makeQuery(id+"F16.imprint","IMPRINT",FACE,{"disambiguationData":[TD([[makeQuery(id+"F16.imprint","IMPRINT",EDGE,{"derivedFrom":subQ0}),1.0]])]});}
            extrude(context, id + "F17", {"entities" : qUnion([Q0, Q1, Q2, Q3, Q4]), "operationType" : NewBodyOperationType.ADD, "oppositeDirection" : true, "depth" : 5 * mm, "offsetDistance" : 25 * mm});
        }
    });
